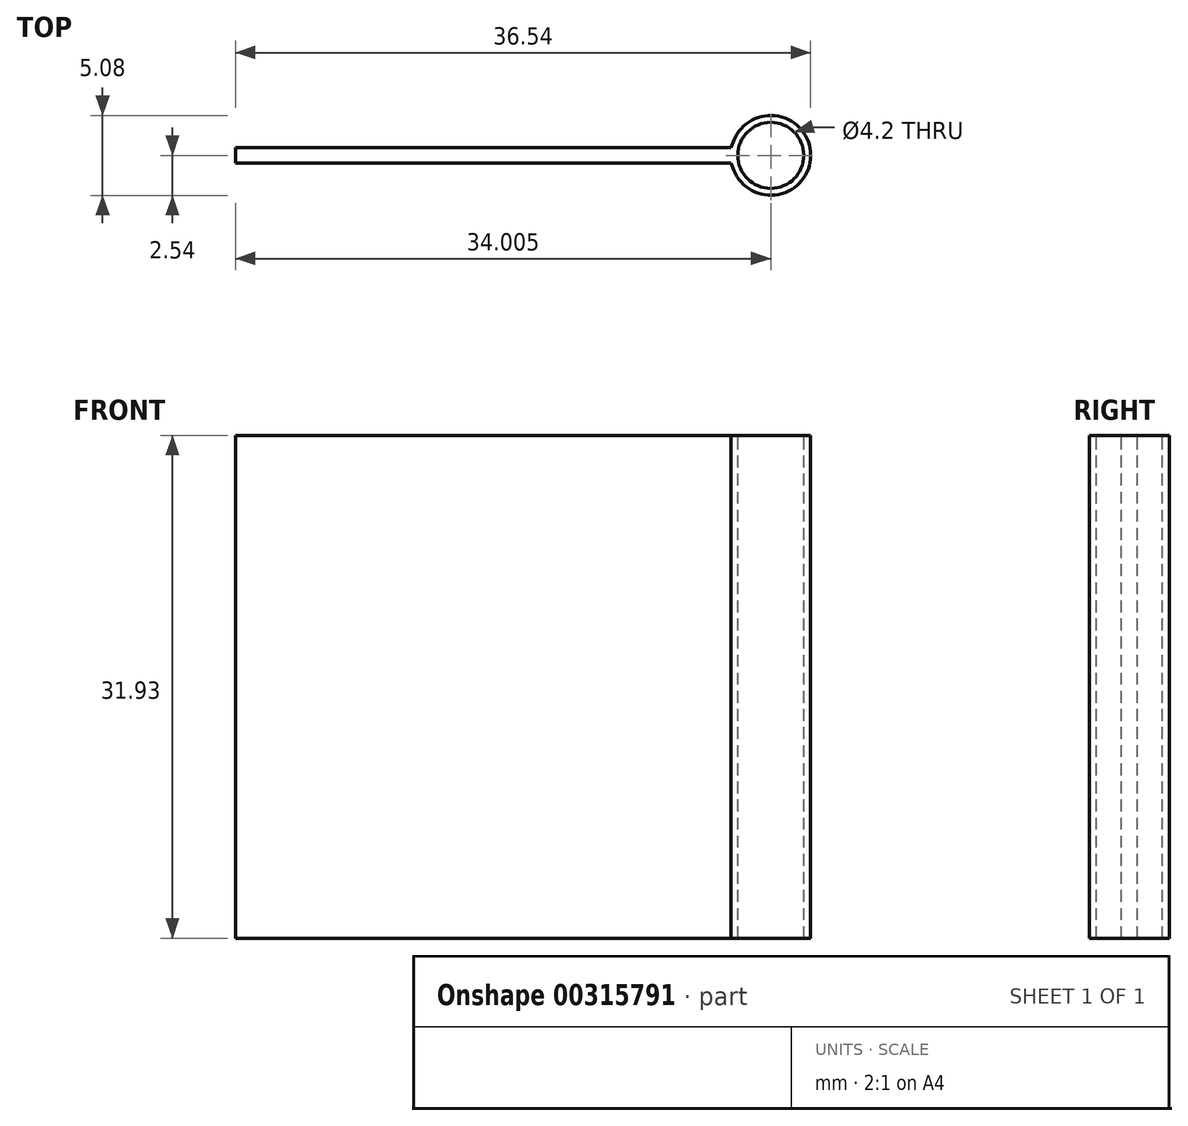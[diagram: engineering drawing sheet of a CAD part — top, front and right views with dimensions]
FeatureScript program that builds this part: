
annotation { "Feature Type Name" : "Feature", "Feature Type Description" : "" }
export const myFeature = defineFeature(function(context is Context, id is Id, definition is map)
    precondition{}
    {
        {
            var Q0;
            Q0=qCreatedBy(makeId("Front.planeOp"),FACE);
            var sketch = newSketch(context, id + "F0", { "sketchPlane" : qUnion([Q0])});
            skLineSegment(sketch, "E0.bottom", {"start": v(-6.18, -7.61) * mm, "end": v(25.29, -7.61) * mm});
            skLineSegment(sketch, "E0.top", {"start": v(-6.18, 24.32) * mm, "end": v(25.29, 24.32) * mm});
            skLineSegment(sketch, "E0.left", {"start": v(-6.18, -7.61) * mm, "end": v(-6.18, 24.32) * mm});
            skLineSegment(sketch, "E0.right", {"start": v(25.29, -7.61) * mm, "end": v(25.29, 24.32) * mm});
            skSolve(sketch);
        }
        {
            var Q0;
            Q0=makeQuery(id+"F0.imprint","IMPRINT",FACE,{"disambiguationData":[TD([[makeQuery(id+"F0.imprint","IMPRINT",EDGE,{"derivedFrom":sQuery(id+"F0.wireOp",EDGE,"E0.bottom")}),1.0]])]});
            extrude(context, id + "F1", {"entities" : qUnion([Q0]), "depth" : 1 * mm});
        }
        {
            var Q0;
            Q0=makeQuery(id+"F1.opExtrude","SWEPT_FACE",FACE,{"disambiguationData":[OSD([sQuery(id+"F0.wireOp",EDGE,"E0.top")])]});
            var sketch = newSketch(context, id + "F2", { "sketchPlane" : qUnion([Q0])});
            skArc(sketch, "E1", {"start": v(25.48, -1.46) * mm, "mid": v(30.36, -0.5) * mm, "end": v(25.48, 0.46) * mm});
            skPoint(sketch, "E1.centerSnap0", {"position": v(25.29, -0.5) * mm});
            skCircle(sketch, "E2", {"center": v(27.82, -0.5) * mm, "radius": 2.1 * mm});
            skLineSegment(sketch, "E3", {"start": v(25.29, -1) * mm, "end": v(25.48, -1.46) * mm});
            skLineSegment(sketch, "E4", {"start": v(25.29, 0) * mm, "end": v(25.48, 0.46) * mm});
            skSolve(sketch);
        }
        {
            var Q0;
            Q0=makeQuery(id+"F2.imprint","IMPRINT",FACE,{"disambiguationData":[TD([[makeQuery(id+"F2.imprint","IMPRINT",EDGE,{"derivedFrom":sQuery(id+"F2.wireOp",EDGE,"E1")}),1.0]])]});
            var Q1;
            Q1=makeQuery(id+"F1.opExtrude","SWEPT_FACE",FACE,{"disambiguationData":[OSD([sQuery(id+"F0.wireOp",EDGE,"E0.bottom")])]});
            extrude(context, id + "F3", {"entities" : qUnion([Q0]), "operationType" : NewBodyOperationType.ADD, "endBound" : BoundingType.UP_TO_SURFACE, "oppositeDirection" : true, "endBoundEntityFace" : qUnion([Q1]), "depth" : 25.4 * mm});
        }
    });
